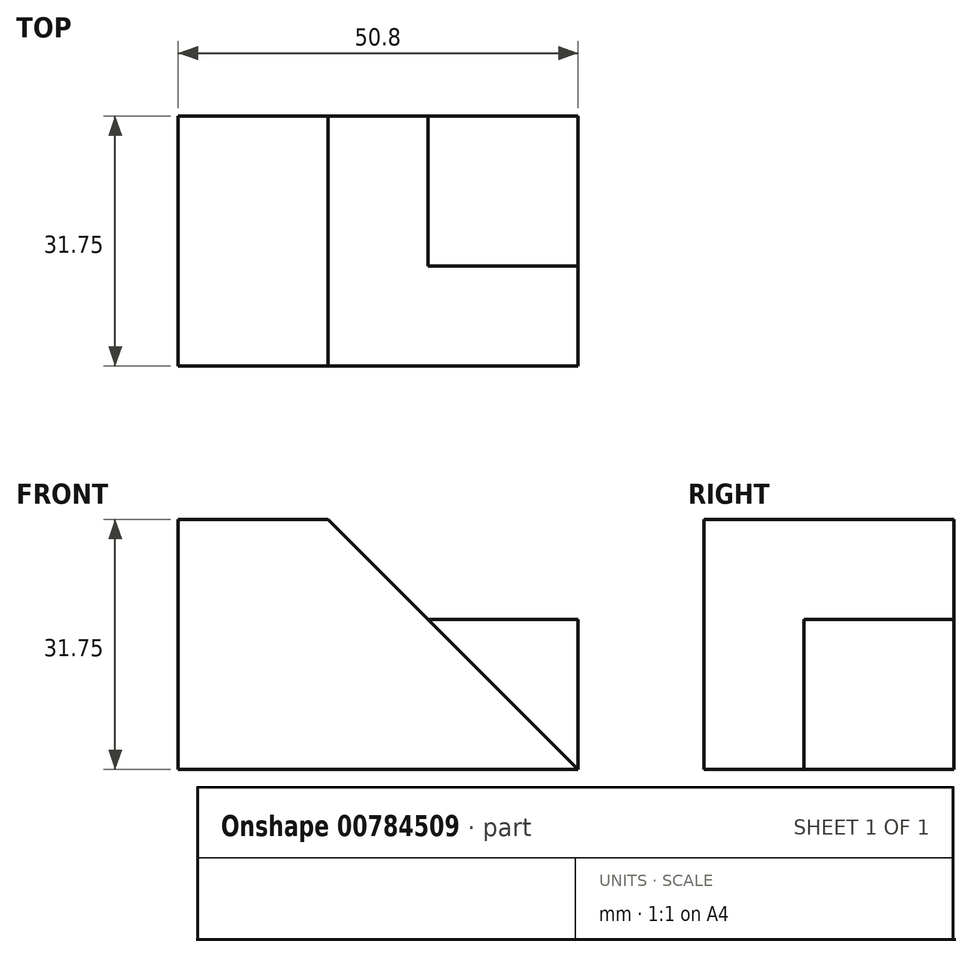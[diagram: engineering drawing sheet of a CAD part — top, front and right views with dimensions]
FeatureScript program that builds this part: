
annotation { "Feature Type Name" : "Feature", "Feature Type Description" : "" }
export const myFeature = defineFeature(function(context is Context, id is Id, definition is map)
    precondition{}
    {
        {
            var Q0;
            Q0=qCreatedBy(makeId("Front.planeOp"),FACE);
            var sketch = newSketch(context, id + "F0", { "sketchPlane" : qUnion([Q0])});
            skLineSegment(sketch, "E0", {"start": v(0, 0) * mm, "end": v(50.8, 0) * mm});
            skLineSegment(sketch, "E1", {"start": v(50.8, 0) * mm, "end": v(50.8, 31.75) * mm});
            skLineSegment(sketch, "E2", {"start": v(50.8, 31.75) * mm, "end": v(0, 31.75) * mm});
            skLineSegment(sketch, "E3", {"start": v(0, 31.75) * mm, "end": v(0, 0) * mm});
            skSolve(sketch);
        }
        {
            var Q0;
            Q0 = qSketchRegion(id + "F0", true);
            extrude(context, id + "F1", {"entities" : qUnion([Q0]), "depth" : 31.75 * mm, "offsetDistance" : 25.4 * mm});
        }
        {
            var Q0;
            Q0=makeQuery(id+"F1.opExtrude","CAP_FACE",FACE,{"disambiguationData":[OSD([sQuery(id+"F0.wireOp",EDGE,"E0"),sQuery(id+"F0.wireOp",EDGE,"E1"),sQuery(id+"F0.wireOp",EDGE,"E2"),sQuery(id+"F0.wireOp",EDGE,"E3")])],"isStart":false});
            var sketch = newSketch(context, id + "F2", { "sketchPlane" : qUnion([Q0])});
            skLineSegment(sketch, "E4", {"start": v(50.8, 31.75) * mm, "end": v(19.05, 31.75) * mm});
            skLineSegment(sketch, "E5", {"start": v(19.05, 31.75) * mm, "end": v(50.8, 0) * mm});
            skLineSegment(sketch, "E6", {"start": v(50.8, 0) * mm, "end": v(50.8, 31.75) * mm});
            skSolve(sketch);
        }
        {
            var Q0;
            Q0=makeQuery(id+"F2.imprint","IMPRINT",FACE,{"disambiguationData":[TD([[makeQuery(id+"F2.imprint","IMPRINT",EDGE,{"derivedFrom":sQuery(id+"F2.wireOp",EDGE,"E4")}),1.0]])]});
            var sketch = newSketch(context, id + "F3", { "sketchPlane" : qUnion([Q0])});
            skSolve(sketch);
        }
        {
            var Q0;
            Q0=makeQuery(id+"F3.imprint","IMPRINT",FACE,{"disambiguationData":[TD([[makeQuery(id+"F3.imprint","IMPRINT",EDGE,{"derivedFrom":makeQuery(id+"F2.imprint","IMPRINT",EDGE,{"derivedFrom":sQuery(id+"F2.wireOp",EDGE,"E4")})}),1.0]])]});
            extrude(context, id + "F4", {"entities" : qUnion([Q0]), "operationType" : NewBodyOperationType.REMOVE, "oppositeDirection" : true, "depth" : 12.7 * mm, "offsetDistance" : 25.4 * mm});
        }
        {
            var Q0;
            Q0=makeQuery(id+"F1.opExtrude","CAP_FACE",FACE,{"disambiguationData":[OSD([sQuery(id+"F0.wireOp",EDGE,"E0"),sQuery(id+"F0.wireOp",EDGE,"E1"),sQuery(id+"F0.wireOp",EDGE,"E2"),sQuery(id+"F0.wireOp",EDGE,"E3")])],"isStart":true});
            var sketch = newSketch(context, id + "F5", { "sketchPlane" : qUnion([Q0])});
            skLineSegment(sketch, "E7", {"start": v(-50.8, 31.75) * mm, "end": v(-19.05, 31.75) * mm});
            skLineSegment(sketch, "E8", {"start": v(-50.8, 31.75) * mm, "end": v(-50.8, 19.05) * mm});
            skLineSegment(sketch, "E9", {"start": v(-50.8, 19.05) * mm, "end": v(-50.8, 31.75) * mm});
            skLineSegment(sketch, "E10", {"start": v(-31.75, 19.05) * mm, "end": v(-50.8, 19.05) * mm});
            skLineSegment(sketch, "E11", {"start": v(-31.75, 19.05) * mm, "end": v(-19.05, 31.75) * mm});
            skSolve(sketch);
        }
        {
            var Q0;
            Q0 = qSketchRegion(id + "F5", true);
            extrude(context, id + "F6", {"entities" : qUnion([Q0]), "operationType" : NewBodyOperationType.REMOVE, "oppositeDirection" : true, "depth" : 19.05 * mm, "offsetDistance" : 25.4 * mm});
        }
    });
